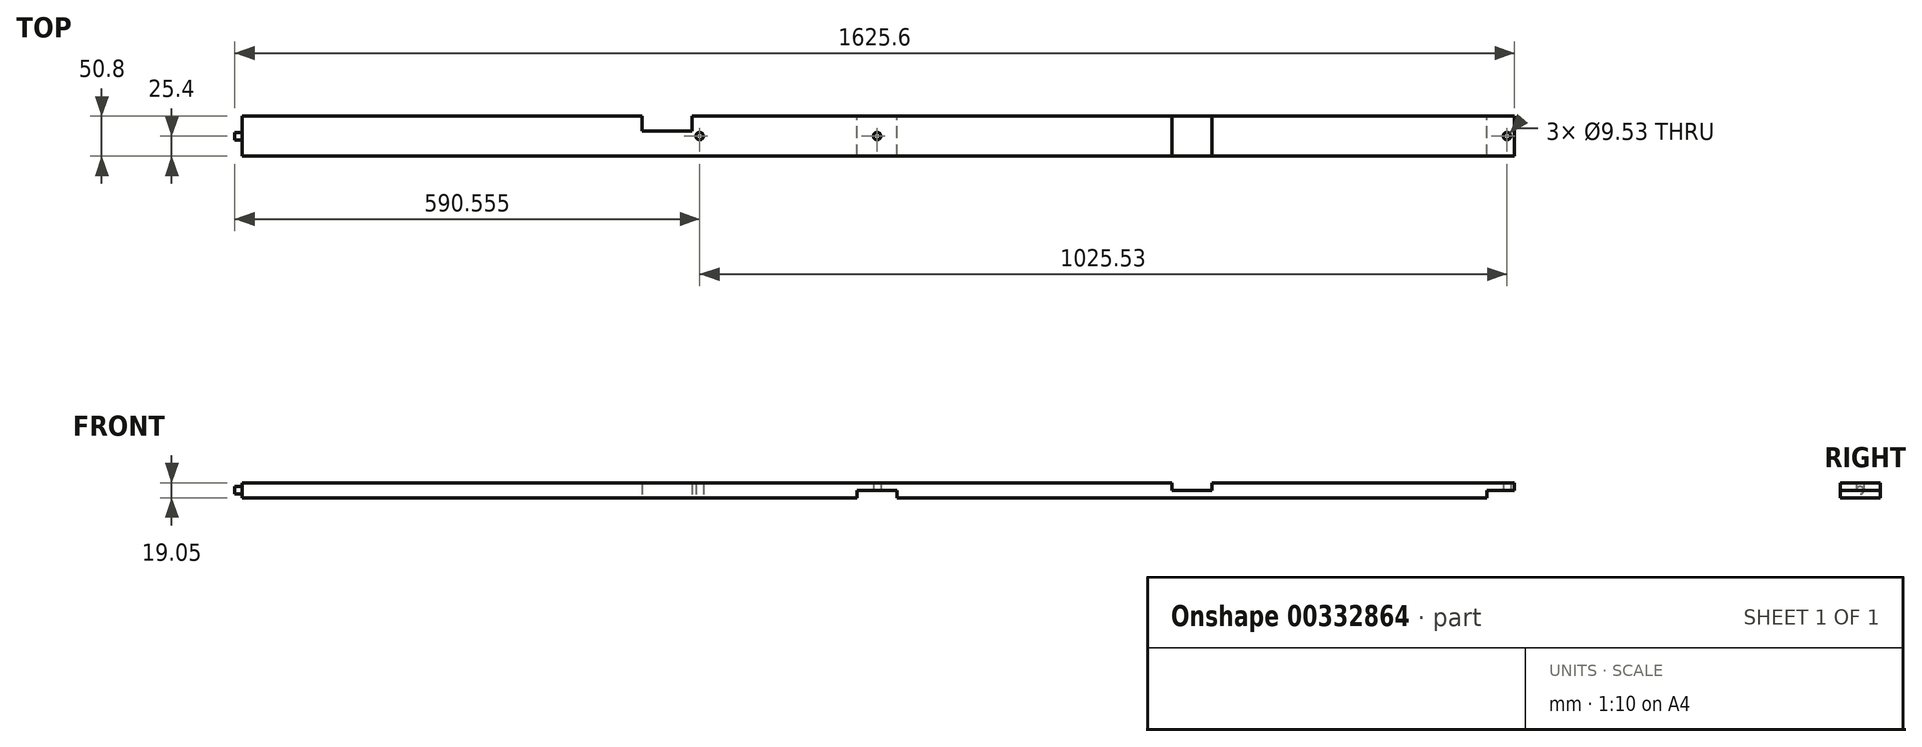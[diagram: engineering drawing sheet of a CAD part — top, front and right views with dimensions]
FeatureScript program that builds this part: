
annotation { "Feature Type Name" : "Feature", "Feature Type Description" : "" }
export const myFeature = defineFeature(function(context is Context, id is Id, definition is map)
    precondition{}
    {
        {
            var Q0;
            Q0=qCreatedBy(makeId("Front.planeOp"),FACE);
            var sketch = newSketch(context, id + "F0", { "sketchPlane" : qUnion([Q0])});
            skLineSegment(sketch, "E0", {"start": v(1616.08, 19.05) * mm, "end": v(0, 19.05) * mm});
            skPoint(sketch, "E1.left.start.orphan", {"position": v(-798.41, -3.82) * mm});
            skLineSegment(sketch, "E2.top", {"start": v(781.05, 9.52) * mm, "end": v(831.85, 9.52) * mm});
            skLineSegment(sketch, "E2.left", {"start": v(781.05, 0) * mm, "end": v(781.05, 9.52) * mm});
            skLineSegment(sketch, "E2.right", {"start": v(831.85, 0) * mm, "end": v(831.85, 9.52) * mm});
            skLineSegment(sketch, "E3.trimOffspring", {"start": v(831.85, 0) * mm, "end": v(1581.15, 0) * mm});
            skLineSegment(sketch, "E4.left", {"start": v(1581.15, 0) * mm, "end": v(1581.15, 9.53) * mm});
            skLineSegment(sketch, "E5.trimOffspring", {"start": v(939.8, 0) * mm, "end": v(939.8, 0) * mm});
            skLineSegment(sketch, "E6.top", {"start": v(1581.15, 9.52) * mm, "end": v(1616.08, 9.52) * mm});
            skPoint(sketch, "E7.orphan", {"position": v(1631.95, 0) * mm});
            skLineSegment(sketch, "E8", {"start": v(0, 0) * mm, "end": v(0, 19.05) * mm});
            skLineSegment(sketch, "E9", {"start": v(781.05, 0) * mm, "end": v(0, 0) * mm});
            skLineSegment(sketch, "E10", {"start": v(1616.08, 19.05) * mm, "end": v(1616.08, 9.53) * mm});
            skSolve(sketch);
        }
        {
            var Q0;
            Q0=qSketchRegion(id+"F0",true);
            extrude(context, id + "F1", {"entities" : qUnion([Q0]), "depth" : 50.8 * mm});
        }
        {
            var Q0;
            Q0=qCreatedBy(makeId("Top.planeOp"),FACE);
            cPlane(context, id + "F2", {"entities" : qUnion([Q0]), "cplaneType" : CPlaneType.OFFSET, "offset" : 9.52 * mm, "width" : 152.4 * mm, "height" : 152.4 * mm});
        }
        {
            var Q0;
            Q0=qCreatedBy(id+"F2.planeOp",FACE);
            var sketch = newSketch(context, id + "F3", { "sketchPlane" : qUnion([Q0])});
            skCircle(sketch, "E11", {"center": v(806.45, -25.4) * mm, "radius": 4.76 * mm});
            skCircle(sketch, "E12", {"center": v(1606.55, -25.4) * mm, "radius": 4.76 * mm});
            skCircle(sketch, "E13", {"center": v(581.02, -25.4) * mm, "radius": 4.76 * mm});
            skLineSegment(sketch, "E14.bottom", {"start": v(508, -19.05) * mm, "end": v(571.5, -19.05) * mm});
            skLineSegment(sketch, "E14.top", {"start": v(508, 82.55) * mm, "end": v(571.5, 82.55) * mm});
            skLineSegment(sketch, "E14.left", {"start": v(508, -19.05) * mm, "end": v(508, 82.55) * mm});
            skLineSegment(sketch, "E14.right", {"start": v(571.5, -19.05) * mm, "end": v(571.5, 82.55) * mm});
            skSolve(sketch);
        }
        {
            var Q0;
            Q0 = qSketchRegion(id + "F3", true);
            extrude(context, id + "F4", {"entities" : qUnion([Q0]), "operationType" : NewBodyOperationType.REMOVE, "endBound" : BoundingType.SYMMETRIC, "depth" : 25.4 * mm});
        }
        {
            var Q0;
            Q0=qCreatedBy(makeId("Right.planeOp"),FACE);
            var sketch = newSketch(context, id + "F5", { "sketchPlane" : qUnion([Q0])});
            skCircle(sketch, "E15", {"center": v(-25.4, 9.53) * mm, "radius": 4.76 * mm});
            skSolve(sketch);
        }
        {
            var Q0;
            Q0 = qSketchRegion(id + "F5", true);
            extrude(context, id + "F6", {"entities" : qUnion([Q0]), "operationType" : NewBodyOperationType.ADD, "oppositeDirection" : true, "depth" : 9.52 * mm});
        }
        {
            var Q0;
            Q0=qCreatedBy(id+"F2.planeOp",FACE);
            var sketch = newSketch(context, id + "F7", { "sketchPlane" : qUnion([Q0])});
            skLineSegment(sketch, "E16", {"start": v(1206.5, 265.5) * mm, "end": v(1206.5, -187.53) * mm, "construction": true});
            skLineSegment(sketch, "E17.bottom", {"start": v(1231.9, 37.08) * mm, "end": v(1181.1, 37.08) * mm});
            skLineSegment(sketch, "E17.top", {"start": v(1231.9, -92.98) * mm, "end": v(1181.1, -92.98) * mm});
            skLineSegment(sketch, "E17.left", {"start": v(1231.9, 37.08) * mm, "end": v(1231.9, -92.98) * mm});
            skLineSegment(sketch, "E17.right", {"start": v(1181.1, 37.08) * mm, "end": v(1181.1, -92.98) * mm});
            skPoint(sketch, "E17.middle", {"position": v(1206.5, -27.95) * mm});
            skSolve(sketch);
        }
        {
            var Q0;
            Q0 = qSketchRegion(id + "F7", true);
            extrude(context, id + "F8", {"entities" : qUnion([Q0]), "operationType" : NewBodyOperationType.REMOVE, "depth" : 25.4 * mm});
        }
    });
